# Revit family: PLL - SECONDA CONSEGNA - ASTA FIGLIO
name_source: partatom
category: Generic Models
revit_build: Autodesk Revit 2017 (Build: 20160225_1515(x64)
units: mm (PartAtom-declared; Revit-internal decimal feet)

## family parameters
Can host rebar = No
Cut with Voids When Loaded = No
Part Type = Normal
Room Calculation Point = No
Round Connector Dimension = Use Diameter
Shared = No

## types (2) — shared parameters

## per-type parameters (varying)
| type | b | h | material | profonditò asta | semi b | semi h |
| 200x1000 | 200 mm  [stored 0.656168 ft] | 1000 mm  [stored 3.28084 ft] | <By Category> | 286 mm | 100 mm  [stored 0.328084 ft] | 500 mm  [stored 1.64042 ft] |
| 1000x200 | 250 mm  [stored 0.82021 ft] | 125 mm  [stored 0.410105 ft] | PLL - 2^ CONSEGNA - WOOD | 3000 mm  [stored 9.84252 ft] | 125 mm  [stored 0.410105 ft] | 63 mm |

note: [stored X ft] marks values corroborated as IEEE doubles in the binary element streams (Revit-internal decimal feet)

## geometry (parser evidence)
native form markers: Sweep x6
no freeform markers — native parametric forms only
